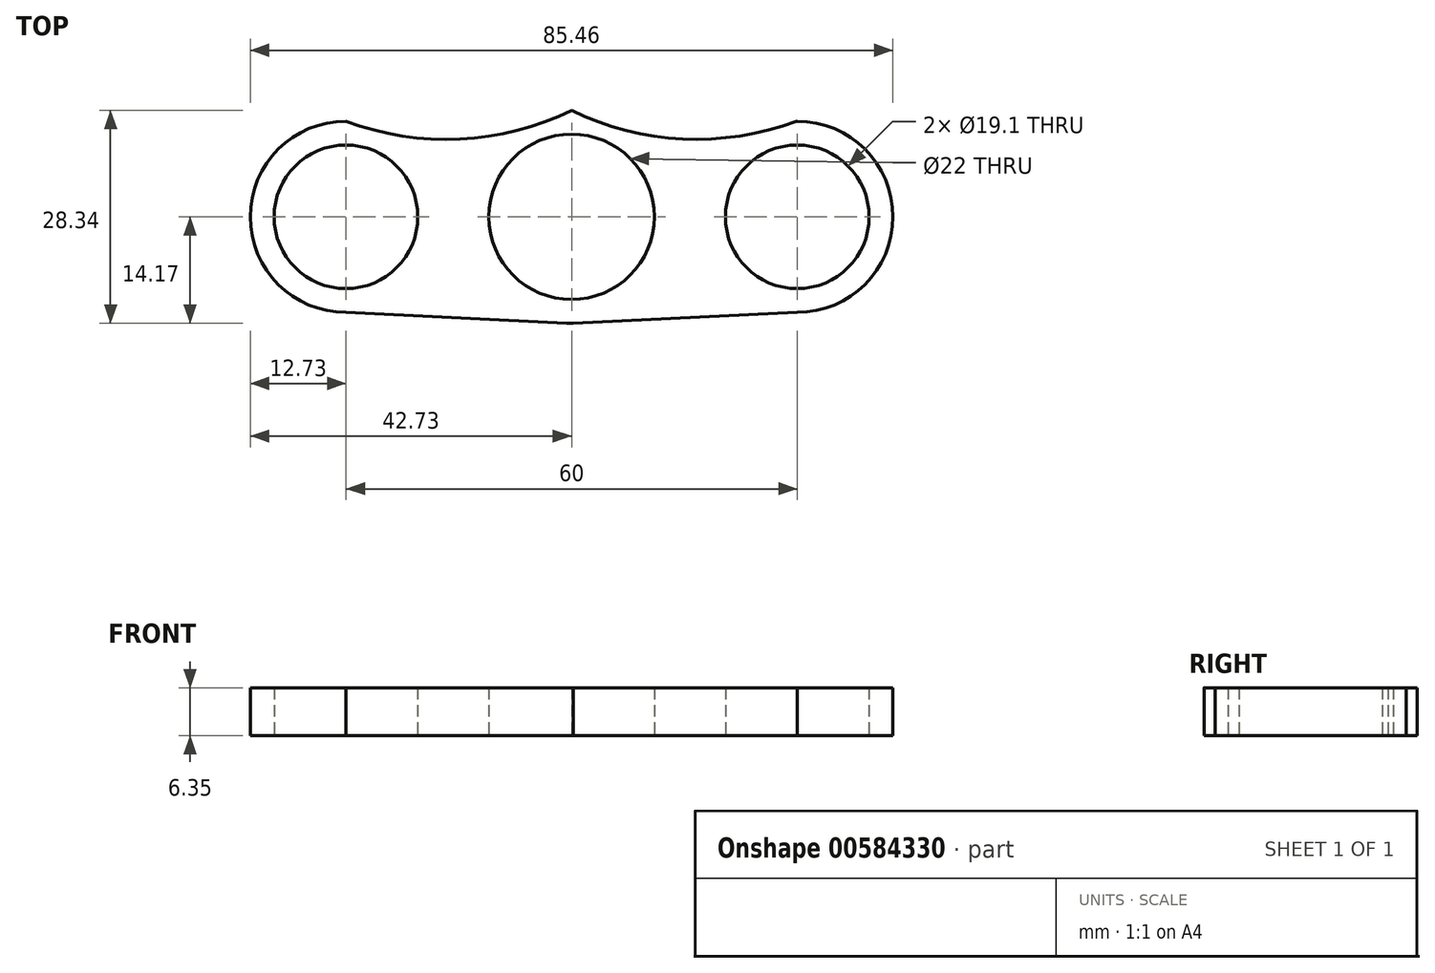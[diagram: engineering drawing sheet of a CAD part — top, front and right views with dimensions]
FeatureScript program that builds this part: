
annotation { "Feature Type Name" : "Feature", "Feature Type Description" : "" }
export const myFeature = defineFeature(function(context is Context, id is Id, definition is map)
    precondition{}
    {
        {
            var Q0;
            Q0=qCreatedBy(makeId("Top.planeOp"),FACE);
            var sketch = newSketch(context, id + "F0", { "sketchPlane" : qUnion([Q0])});
            skCircle(sketch, "E0", {"center": v(0, 0) * mm, "radius": 11 * mm});
            skCircle(sketch, "E1.0", {"center": v(0, 0) * mm, "radius": 14.18 * mm});
            skLineSegment(sketch, "E2", {"start": v(0, 0) * mm, "end": v(30, 0) * mm});
            skCircle(sketch, "E3", {"center": v(30, 0) * mm, "radius": 9.55 * mm});
            skCircle(sketch, "E4.0", {"center": v(30, 0) * mm, "radius": 12.73 * mm});
            skLineSegment(sketch, "E5", {"start": v(0, 0) * mm, "end": v(-30, 0) * mm});
            skCircle(sketch, "E6", {"center": v(-30, 0) * mm, "radius": 9.55 * mm});
            skCircle(sketch, "E7.0", {"center": v(-30, 0) * mm, "radius": 12.73 * mm});
            skLineSegment(sketch, "E8", {"start": v(-30, 12.72) * mm, "end": v(0, 14.18) * mm});
            skLineSegment(sketch, "E9", {"start": v(0, 14.18) * mm, "end": v(30, 12.72) * mm});
            skLineSegment(sketch, "E10", {"start": v(-30, -12.73) * mm, "end": v(0, -14.2) * mm});
            skLineSegment(sketch, "E11", {"start": v(30, -12.72) * mm, "end": v(0.24, -14.17) * mm});
            skSolve(sketch);
        }
        {
            var Q0;
            {var subQ0=sQuery(id+"F0.wireOp",EDGE,"ZYrkaDll-I0XF-CetN-NEAo-xjh4SI9szIyb");var subQ1=sQuery(id+"F0.wireOp",EDGE,"E1.0");var subQ2=makeQuery(id+"F0.imprint","INTERSECT",VERTEX,{"derivedFrom":[subQ1,subQ0]});Q0=makeQuery(id+"F0.imprint","IMPRINT",FACE,{"disambiguationData":[TD([[makeQuery(id+"F0.imprint","IMPRINT",EDGE,{"disambiguationData":[TD([[subQ2,1.0]])],"derivedFrom":subQ1}),-1.0]])]});}
            var Q1;
            Q1=makeQuery(id+"F0.imprint","IMPRINT",FACE,{"disambiguationData":[TD([[makeQuery(id+"F0.imprint","IMPRINT",EDGE,{"derivedFrom":sQuery(id+"F0.wireOp",EDGE,"E3")}),-1.0]])]});
            var Q2;
            {var subQ0=sQuery(id+"F0.wireOp",EDGE,"E2");var subQ1=sQuery(id+"F0.wireOp",EDGE,"E1.0");var subQ2=makeQuery(id+"F0.imprint","INTERSECT",VERTEX,{"derivedFrom":[subQ1,subQ0]});Q2=makeQuery(id+"F0.imprint","IMPRINT",FACE,{"disambiguationData":[TD([[makeQuery(id+"F0.imprint","IMPRINT",EDGE,{"disambiguationData":[TD([[subQ2,1.0]])],"derivedFrom":subQ1}),-1.0]])]});}
            var Q3;
            Q3=makeQuery(id+"F0.imprint","IMPRINT",FACE,{"disambiguationData":[TD([[makeQuery(id+"F0.imprint","IMPRINT",EDGE,{"derivedFrom":sQuery(id+"F0.wireOp",EDGE,"E0")}),-1.0]])]});
            var Q4;
            Q4=makeQuery(id+"F0.imprint","IMPRINT",FACE,{"disambiguationData":[TD([[makeQuery(id+"F0.imprint","IMPRINT",EDGE,{"derivedFrom":sQuery(id+"F0.wireOp",EDGE,"61101760-2203-494f-9f1b-4a81e298778f")}),-1.0]])]});
            var Q5;
            {var subQ0=sQuery(id+"F0.wireOp",EDGE,"ZYrkaDll-I0XF-CetN-NEAo-xjh4SI9szIyb");var subQ1=sQuery(id+"F0.wireOp",EDGE,"E1.0");var subQ2=makeQuery(id+"F0.imprint","INTERSECT",VERTEX,{"derivedFrom":[subQ1,subQ0]});Q5=makeQuery(id+"F0.imprint","IMPRINT",FACE,{"disambiguationData":[TD([[makeQuery(id+"F0.imprint","IMPRINT",EDGE,{"disambiguationData":[TD([[subQ2,-1.0]])],"derivedFrom":subQ1}),-1.0]])]});}
            var Q6;
            Q6=makeQuery(id+"F0.imprint","IMPRINT",FACE,{"disambiguationData":[TD([[makeQuery(id+"F0.imprint","IMPRINT",EDGE,{"derivedFrom":sQuery(id+"F0.wireOp",EDGE,"E6")}),-1.0]])]});
            extrude(context, id + "F1", {"entities" : qUnion([Q0, Q1, Q2, Q3, Q4, Q5, Q6]), "depth" : 6.35 * mm, "offsetDistance" : 25.4 * mm});
        }
        {
            var Q0;
            Q0=qCreatedBy(makeId("Top.planeOp"),FACE);
            var sketch = newSketch(context, id + "F2", { "sketchPlane" : qUnion([Q0])});
            skPoint(sketch, "E12.0", {"position": v(-30, 12.73) * mm});
            skPoint(sketch, "E13.0", {"position": v(-30, -12.73) * mm});
            skPoint(sketch, "E14.0", {"position": v(30, -12.73) * mm});
            skPoint(sketch, "E15.0", {"position": v(30, 12.72) * mm});
            skPoint(sketch, "E16.0", {"position": v(0, 14.18) * mm});
            skPoint(sketch, "E17.0", {"position": v(0.24, -14.17) * mm});
            skCircle(sketch, "E18", {"center": v(-16.66, 47.82) * mm, "radius": 37.55 * mm});
            skPoint(sketch, "E18.third.point", {"position": v(-16.93, 10.28) * mm});
            skCircle(sketch, "E19", {"center": v(16.59, 47.82) * mm, "radius": 37.51 * mm});
            skSolve(sketch);
        }
        {
            var Q0;
            {var subQ0=sQuery(id+"F2.wireOp",EDGE,"E19");var subQ1=sQuery(id+"F2.wireOp",EDGE,"E18");var subQ2=makeQuery(id+"F2.imprint","INTERSECT",VERTEX,{"disambiguationData":[OD(0.0)],"derivedFrom":[subQ1,subQ0]});Q0=makeQuery(id+"F2.imprint","IMPRINT",FACE,{"disambiguationData":[TD([[makeQuery(id+"F2.imprint","IMPRINT",EDGE,{"disambiguationData":[TD([[subQ2,1.0]])],"derivedFrom":subQ1}),1.0]])]});}
            var Q1;
            {var subQ0=sQuery(id+"F2.wireOp",EDGE,"E19");var subQ1=sQuery(id+"F2.wireOp",EDGE,"E18");var subQ2=makeQuery(id+"F2.imprint","INTERSECT",VERTEX,{"disambiguationData":[OD(0.0)],"derivedFrom":[subQ1,subQ0]});Q1=makeQuery(id+"F2.imprint","IMPRINT",FACE,{"disambiguationData":[TD([[makeQuery(id+"F2.imprint","IMPRINT",EDGE,{"disambiguationData":[TD([[subQ2,-1.0]])],"derivedFrom":subQ1}),1.0]])]});}
            var Q2;
            {var subQ0=sQuery(id+"F2.wireOp",EDGE,"E19");var subQ1=sQuery(id+"F2.wireOp",EDGE,"E18");var subQ2=makeQuery(id+"F2.imprint","INTERSECT",VERTEX,{"disambiguationData":[OD(0.0)],"derivedFrom":[subQ1,subQ0]});Q2=makeQuery(id+"F2.imprint","IMPRINT",FACE,{"disambiguationData":[TD([[makeQuery(id+"F2.imprint","IMPRINT",EDGE,{"disambiguationData":[TD([[subQ2,-1.0]])],"derivedFrom":subQ1}),-1.0]])]});}
            extrude(context, id + "F3", {"entities" : qUnion([Q0, Q1, Q2]), "operationType" : NewBodyOperationType.REMOVE, "depth" : 25 * mm, "offsetDistance" : 25 * mm});
        }
    });
